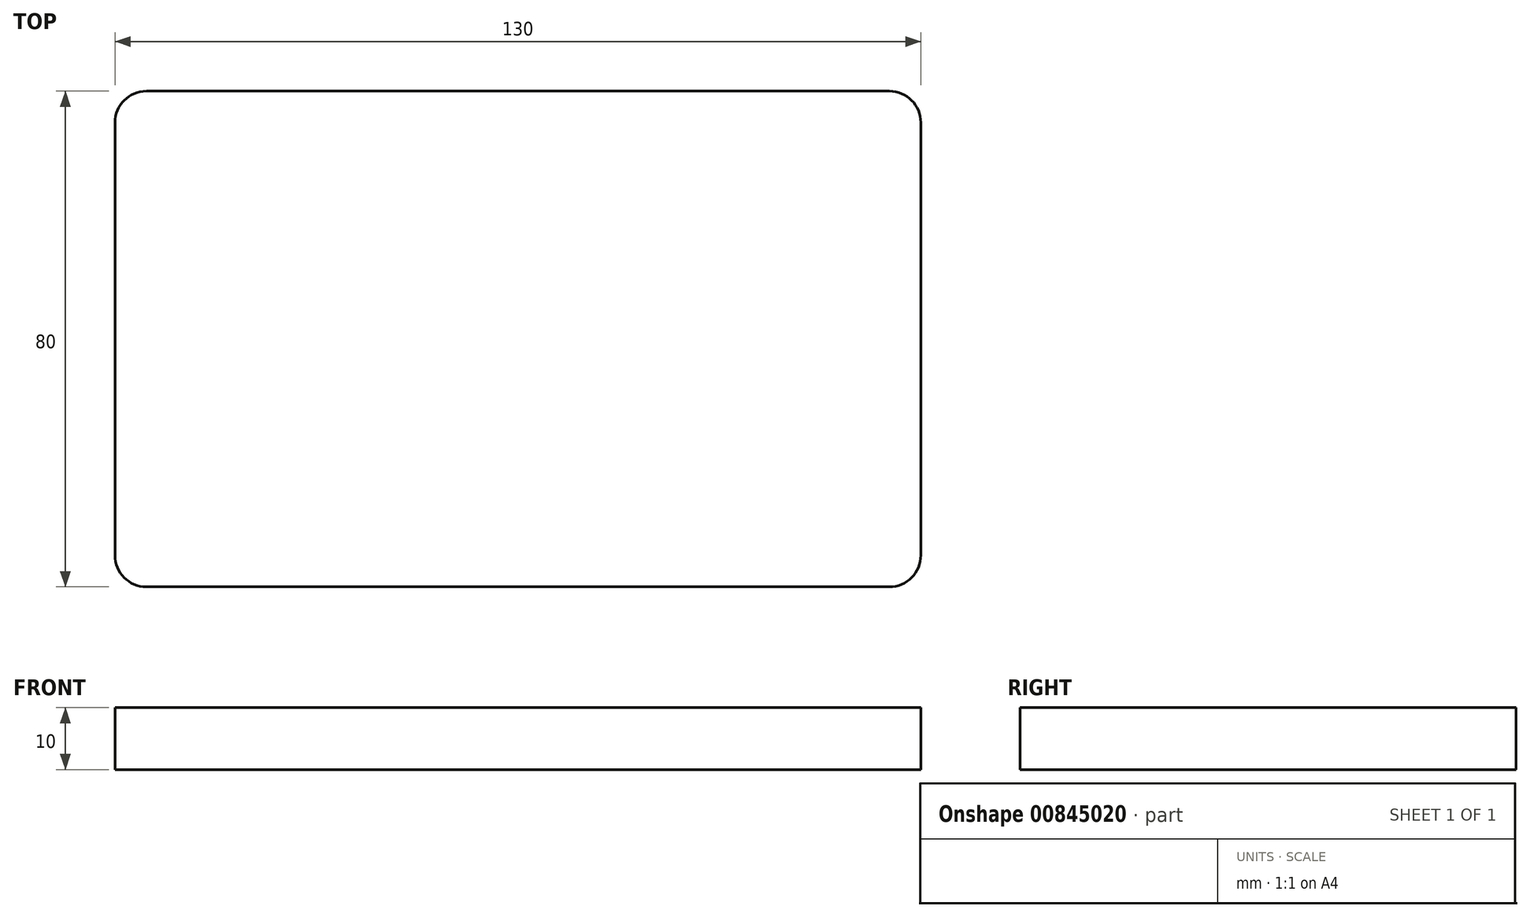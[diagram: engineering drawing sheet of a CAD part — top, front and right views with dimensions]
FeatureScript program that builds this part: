
annotation { "Feature Type Name" : "Feature", "Feature Type Description" : "" }
export const myFeature = defineFeature(function(context is Context, id is Id, definition is map)
    precondition{}
    {
        {
            var Q0;
            Q0=qCreatedBy(makeId("Top.planeOp"),FACE);
            var sketch = newSketch(context, id + "F0", { "sketchPlane" : qUnion([Q0])});
            skLineSegment(sketch, "E0.bottom", {"start": v(0, 0) * mm, "end": v(-130, 0) * mm});
            skLineSegment(sketch, "E0.top", {"start": v(0, 80) * mm, "end": v(-130, 80) * mm});
            skLineSegment(sketch, "E0.left", {"start": v(0, 0) * mm, "end": v(0, 80) * mm});
            skLineSegment(sketch, "E0.right", {"start": v(-130, 0) * mm, "end": v(-130, 80) * mm});
            skSolve(sketch);
        }
        {
            var Q0;
            Q0=makeQuery(id+"F0.imprint","IMPRINT",FACE,{"disambiguationData":[TD([[makeQuery(id+"F0.imprint","IMPRINT",EDGE,{"derivedFrom":sQuery(id+"F0.wireOp",EDGE,"E0.bottom")}),-1.0]])]});
            extrude(context, id + "F1", {"entities" : qUnion([Q0]), "oppositeDirection" : true, "depth" : 10 * mm, "offsetDistance" : 25.4 * mm});
        }
        {
            var Q0;
            Q0=makeQuery(id+"F1.opExtrude","SWEPT_EDGE",EDGE,{"disambiguationData":[OSD([sQuery(id+"F0.wireOp",EDGE,"E0.top"),sQuery(id+"F0.wireOp",EDGE,"E0.right")])]});
            var Q1;
            Q1=makeQuery(id+"F1.opExtrude","SWEPT_EDGE",EDGE,{"disambiguationData":[OSD([sQuery(id+"F0.wireOp",EDGE,"E0.top"),sQuery(id+"F0.wireOp",EDGE,"E0.left")])]});
            var Q2;
            Q2=makeQuery(id+"F1.opExtrude","SWEPT_EDGE",EDGE,{"disambiguationData":[OSD([sQuery(id+"F0.wireOp",EDGE,"E0.bottom"),sQuery(id+"F0.wireOp",EDGE,"E0.left")])]});
            var Q3;
            Q3=makeQuery(id+"F1.opExtrude","SWEPT_EDGE",EDGE,{"disambiguationData":[OSD([sQuery(id+"F0.wireOp",EDGE,"E0.bottom"),sQuery(id+"F0.wireOp",EDGE,"E0.right")])]});
            fillet(context, id + "F2", {"entities" : qUnion([Q0, Q1, Q2, Q3]), "radius" : 5.08 * mm, "tangentPropagation" : true, "allowEdgeOverflow" : false});
        }
    });
